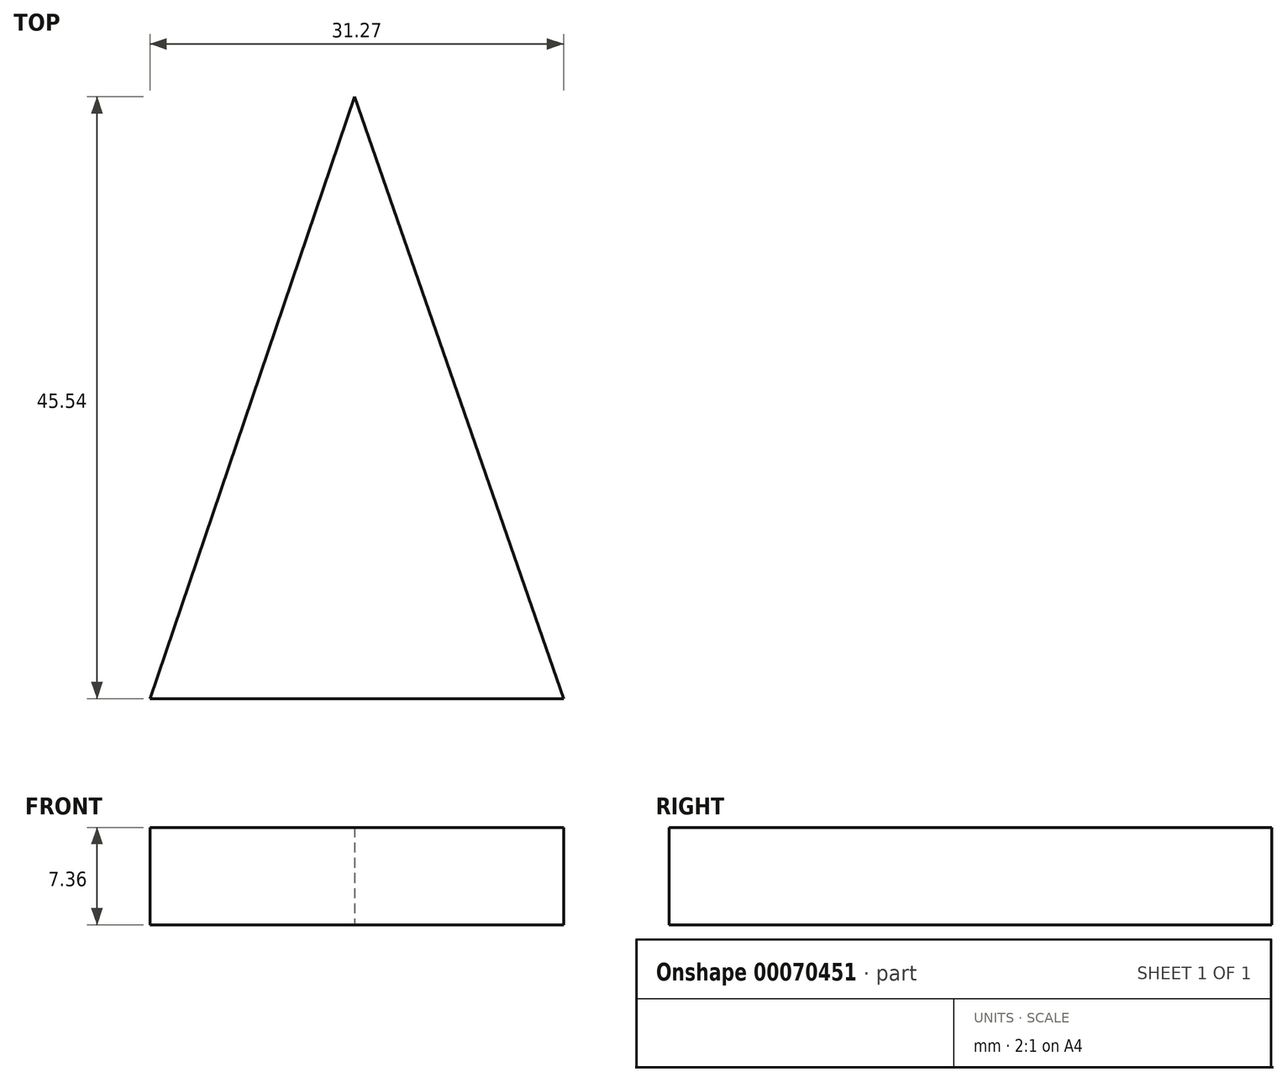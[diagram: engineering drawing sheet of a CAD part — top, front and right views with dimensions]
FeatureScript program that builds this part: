
annotation { "Feature Type Name" : "Feature", "Feature Type Description" : "" }
export const myFeature = defineFeature(function(context is Context, id is Id, definition is map)
    precondition{}
    {
        {
            var Q0;
            Q0=qCreatedBy(makeId("Top.planeOp"),FACE);
            var sketch = newSketch(context, id + "F0", { "sketchPlane" : qUnion([Q0])});
            skLineSegment(sketch, "E0", {"start": v(-40.69, 36.9) * mm, "end": v(-56.17, -8.65) * mm});
            skLineSegment(sketch, "E1", {"start": v(-40.69, 36.9) * mm, "end": v(-24.9, -8.65) * mm});
            skLineSegment(sketch, "E2", {"start": v(-24.9, -8.65) * mm, "end": v(-56.17, -8.65) * mm});
            skSolve(sketch);
        }
        {
            var Q0;
            Q0=makeQuery(id+"F0.imprint","IMPRINT",FACE,{"disambiguationData":[TD([[makeQuery(id+"F0.imprint","IMPRINT",EDGE,{"derivedFrom":sQuery(id+"F0.wireOp",EDGE,"E0")}),1.0]])]});
            extrude(context, id + "F1", {"entities" : qUnion([Q0]), "depth" : 7.36 * mm});
        }
    });
